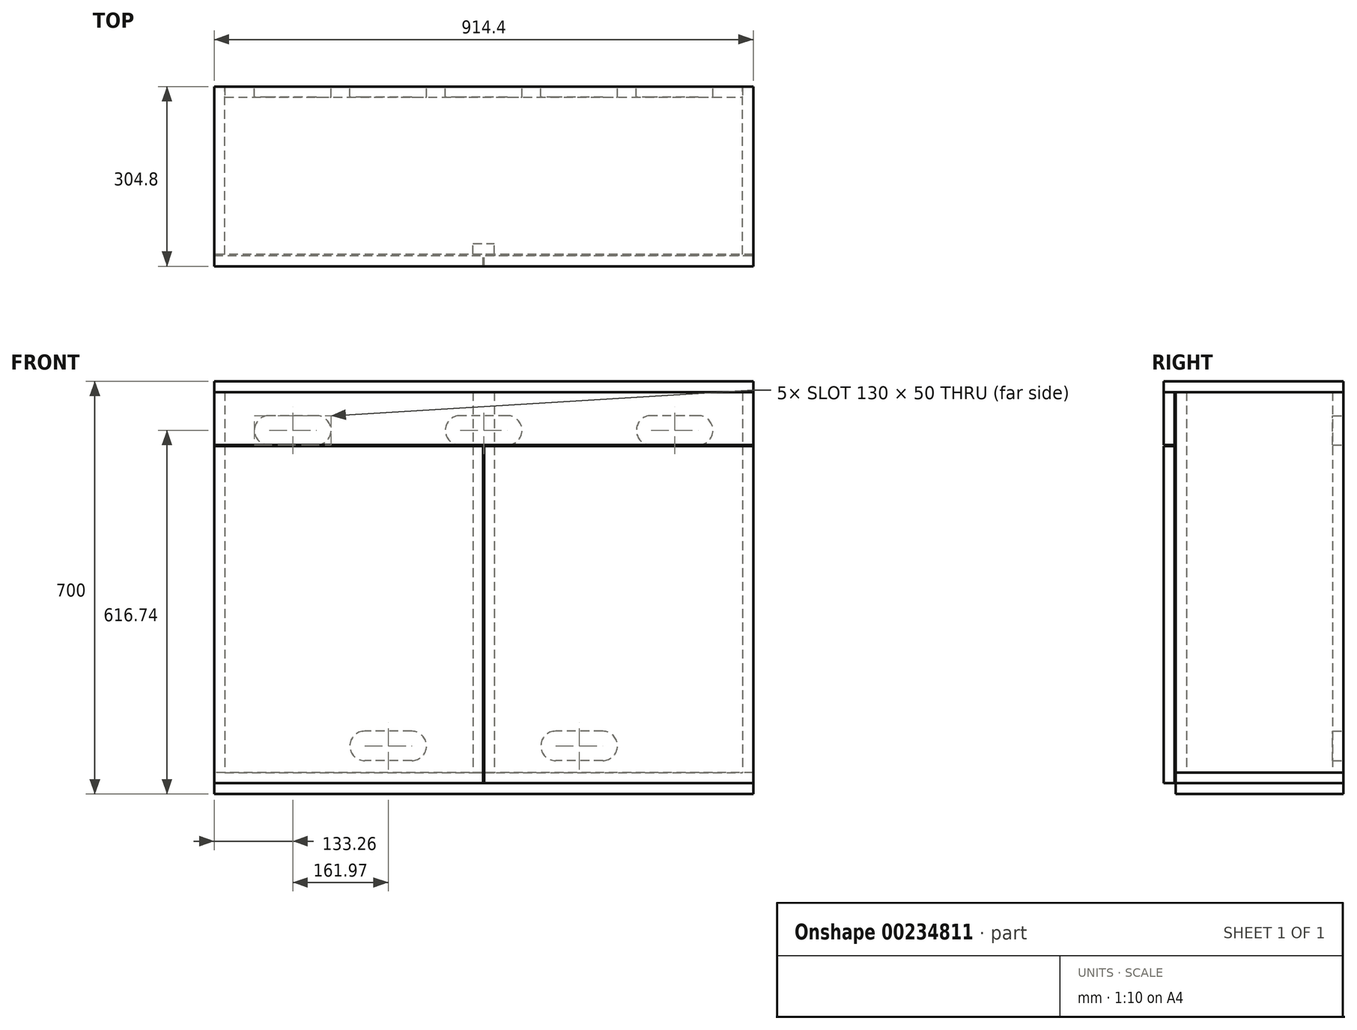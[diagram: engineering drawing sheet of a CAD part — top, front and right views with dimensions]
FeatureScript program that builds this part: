
annotation { "Feature Type Name" : "Feature", "Feature Type Description" : "" }
export const myFeature = defineFeature(function(context is Context, id is Id, definition is map)
    precondition{}
    {
        {
            var Q0;
            Q0=qCreatedBy(makeId("Top.planeOp"),FACE);
            var sketch = newSketch(context, id + "F0", { "sketchPlane" : qUnion([Q0])});
            skLineSegment(sketch, "E0.bottom", {"start": v(457.2, 142.27) * mm, "end": v(-457.2, 142.27) * mm});
            skLineSegment(sketch, "E0.top", {"start": v(457.2, -142.27) * mm, "end": v(-457.2, -142.27) * mm});
            skLineSegment(sketch, "E0.left", {"start": v(457.2, 142.27) * mm, "end": v(457.2, -142.27) * mm});
            skLineSegment(sketch, "E0.right", {"start": v(-457.2, 142.27) * mm, "end": v(-457.2, -142.27) * mm});
            skPoint(sketch, "E0.middle", {"position": v(0, 0) * mm});
            skSolve(sketch);
        }
        {
            var Q0;
            Q0=makeQuery(id+"F0.imprint","IMPRINT",FACE,{"disambiguationData":[TD([[makeQuery(id+"F0.imprint","IMPRINT",EDGE,{"derivedFrom":sQuery(id+"F0.wireOp",EDGE,"E0.bottom")}),1.0]])]});
            extrude(context, id + "F1", {"entities" : qUnion([Q0]), "depth" : 18.26 * mm, "offsetDistance" : 25 * mm});
        }
        {
            var Q0;
            Q0=makeQuery(id+"F1.opExtrude","CAP_FACE",FACE,{"disambiguationData":[OSD([sQuery(id+"F0.wireOp",EDGE,"E0.bottom"),sQuery(id+"F0.wireOp",EDGE,"E0.top"),sQuery(id+"F0.wireOp",EDGE,"E0.left"),sQuery(id+"F0.wireOp",EDGE,"E0.right")])],"isStart":false});
            var sketch = newSketch(context, id + "F2", { "sketchPlane" : qUnion([Q0])});
            skLineSegment(sketch, "E1.bottom", {"start": v(438.94, -142.27) * mm, "end": v(457.2, -142.27) * mm});
            skLineSegment(sketch, "E1.top", {"start": v(438.94, 142.27) * mm, "end": v(457.2, 142.27) * mm});
            skLineSegment(sketch, "E1.left", {"start": v(438.94, -142.27) * mm, "end": v(438.94, 142.27) * mm});
            skLineSegment(sketch, "E1.right", {"start": v(457.2, -142.27) * mm, "end": v(457.2, 142.27) * mm});
            skLineSegment(sketch, "E2.MirrorCS", {"start": v(-438.94, 142.27) * mm, "end": v(-457.2, 142.27) * mm});
            skLineSegment(sketch, "E3.MirrorCS", {"start": v(-438.94, -142.27) * mm, "end": v(-457.2, -142.27) * mm});
            skLineSegment(sketch, "E4.MirrorCS", {"start": v(-457.2, -142.27) * mm, "end": v(-457.2, 142.27) * mm});
            skLineSegment(sketch, "E5.MirrorCS", {"start": v(-438.94, -142.27) * mm, "end": v(-438.94, 142.27) * mm});
            skSolve(sketch);
        }
        {
            var Q0;
            Q0 = qSketchRegion(id + "F2", true);
            extrude(context, id + "F3", {"entities" : qUnion([Q0]), "depth" : 645.22 * mm, "offsetDistance" : 25 * mm});
        }
        {
            var Q0;
            Q0=makeQuery(id+"F1.opExtrude","CAP_FACE",FACE,{"disambiguationData":[OSD([sQuery(id+"F0.wireOp",EDGE,"E0.bottom"),sQuery(id+"F0.wireOp",EDGE,"E0.top"),sQuery(id+"F0.wireOp",EDGE,"E0.left"),sQuery(id+"F0.wireOp",EDGE,"E0.right")])],"isStart":false});
            var sketch = newSketch(context, id + "F4", { "sketchPlane" : qUnion([Q0])});
            skLineSegment(sketch, "E6.bottom", {"start": v(-438.94, 142.27) * mm, "end": v(438.94, 142.27) * mm});
            skLineSegment(sketch, "E6.top", {"start": v(-438.94, 124.01) * mm, "end": v(438.94, 124.01) * mm});
            skLineSegment(sketch, "E6.left", {"start": v(-438.94, 142.27) * mm, "end": v(-438.94, 124.01) * mm});
            skLineSegment(sketch, "E6.right", {"start": v(438.94, 142.27) * mm, "end": v(438.94, 124.01) * mm});
            skSolve(sketch);
        }
        {
            var Q0;
            Q0 = qSketchRegion(id + "F4", true);
            var Q1;
            Q1=makeQuery(id+"F3.opExtrude","CAP_FACE",FACE,{"disambiguationData":[OSD([sQuery(id+"F2.wireOp",EDGE,"E1.bottom"),sQuery(id+"F2.wireOp",EDGE,"E1.top"),sQuery(id+"F2.wireOp",EDGE,"E1.left"),sQuery(id+"F2.wireOp",EDGE,"E1.right")])],"isStart":false});
            extrude(context, id + "F5", {"entities" : qUnion([Q0]), "endBound" : BoundingType.UP_TO_SURFACE, "depth" : 25 * mm, "endBoundEntityFace" : qUnion([Q1]), "offsetDistance" : 25 * mm});
        }
        {
            var Q0;
            Q0=makeQuery(id+"F1.opExtrude","CAP_FACE",FACE,{"disambiguationData":[OSD([sQuery(id+"F0.wireOp",EDGE,"E0.bottom"),sQuery(id+"F0.wireOp",EDGE,"E0.top"),sQuery(id+"F0.wireOp",EDGE,"E0.left"),sQuery(id+"F0.wireOp",EDGE,"E0.right")])],"isStart":false});
            var sketch = newSketch(context, id + "F6", { "sketchPlane" : qUnion([Q0])});
            skLineSegment(sketch, "E7.bottom", {"start": v(-18.26, -142.27) * mm, "end": v(18.26, -142.27) * mm});
            skLineSegment(sketch, "E7.top", {"start": v(-18.26, -124.01) * mm, "end": v(18.26, -124.01) * mm});
            skLineSegment(sketch, "E7.left", {"start": v(-18.26, -142.27) * mm, "end": v(-18.26, -124.01) * mm});
            skLineSegment(sketch, "E7.right", {"start": v(18.26, -142.27) * mm, "end": v(18.26, -124.01) * mm});
            skLineSegment(sketch, "E8", {"start": v(0, 0) * mm, "end": v(0, -142.27) * mm, "construction": true});
            skSolve(sketch);
        }
        {
            var Q0;
            Q0 = qSketchRegion(id + "F6", true);
            var Q1;
            Q1=makeQuery(id+"F5.opExtrude","CAP_FACE",FACE,{"disambiguationData":[OSD([sQuery(id+"F4.wireOp",EDGE,"E6.bottom"),sQuery(id+"F4.wireOp",EDGE,"E6.top"),sQuery(id+"F4.wireOp",EDGE,"E6.left"),sQuery(id+"F4.wireOp",EDGE,"E6.right")])],"isStart":false});
            extrude(context, id + "F7", {"entities" : qUnion([Q0]), "endBound" : BoundingType.UP_TO_SURFACE, "depth" : 25 * mm, "endBoundEntityFace" : qUnion([Q1]), "offsetDistance" : 25 * mm});
        }
        {
            var Q0;
            Q0=makeQuery(id+"F1.opExtrude","CAP_FACE",FACE,{"disambiguationData":[OSD([sQuery(id+"F0.wireOp",EDGE,"E0.bottom"),sQuery(id+"F0.wireOp",EDGE,"E0.top"),sQuery(id+"F0.wireOp",EDGE,"E0.left"),sQuery(id+"F0.wireOp",EDGE,"E0.right")])],"isStart":true});
            extrude(context, id + "F8", {"entities" : qUnion([Q0]), "depth" : 18.26 * mm, "offsetDistance" : 25 * mm});
        }
        {
            var Q0;
            Q0=makeQuery(id+"F3.opExtrude","SWEPT_FACE",FACE,{"disambiguationData":[OSD([sQuery(id+"F2.wireOp",EDGE,"E3.MirrorCS")])]});
            cPlane(context, id + "F9", {"entities" : qUnion([Q0]), "cplaneType" : CPlaneType.OFFSET, "offset" : 2 * mm, "width" : 150 * mm, "height" : 150 * mm});
        }
        {
            var Q0;
            Q0=qCreatedBy(id+"F9.planeOp",FACE);
            var sketch = newSketch(context, id + "F10", { "sketchPlane" : qUnion([Q0])});
            skLineSegment(sketch, "E9.bottom", {"start": v(-457.2, 663.48) * mm, "end": v(457.2, 663.48) * mm});
            skLineSegment(sketch, "E9.top", {"start": v(-457.2, 573.48) * mm, "end": v(457.2, 573.48) * mm});
            skLineSegment(sketch, "E9.left", {"start": v(-457.2, 663.48) * mm, "end": v(-457.2, 573.48) * mm});
            skLineSegment(sketch, "E9.right", {"start": v(457.2, 663.48) * mm, "end": v(457.2, 573.48) * mm});
            skSolve(sketch);
        }
        {
            var Q0;
            Q0 = qSketchRegion(id + "F10", true);
            extrude(context, id + "F11", {"entities" : qUnion([Q0]), "depth" : 18.26 * mm, "offsetDistance" : 25 * mm});
        }
        {
            var Q0;
            Q0=makeQuery(id+"F3.opExtrude","CAP_FACE",FACE,{"disambiguationData":[OSD([sQuery(id+"F2.wireOp",EDGE,"E2.MirrorCS"),sQuery(id+"F2.wireOp",EDGE,"E3.MirrorCS"),sQuery(id+"F2.wireOp",EDGE,"E4.MirrorCS"),sQuery(id+"F2.wireOp",EDGE,"E5.MirrorCS")])],"isStart":false});
            var sketch = newSketch(context, id + "F12", { "sketchPlane" : qUnion([Q0])});
            skLineSegment(sketch, "E10.bottom", {"start": v(-457.2, 142.27) * mm, "end": v(457.2, 142.27) * mm});
            skLineSegment(sketch, "E10.top", {"start": v(-457.2, -162.53) * mm, "end": v(457.2, -162.53) * mm});
            skLineSegment(sketch, "E10.left", {"start": v(-457.2, 142.27) * mm, "end": v(-457.2, -162.53) * mm});
            skLineSegment(sketch, "E10.right", {"start": v(457.2, 142.27) * mm, "end": v(457.2, -162.53) * mm});
            skSolve(sketch);
        }
        {
            var Q0;
            Q0 = qSketchRegion(id + "F12", true);
            extrude(context, id + "F13", {"entities" : qUnion([Q0]), "depth" : 18.26 * mm, "offsetDistance" : 25 * mm});
        }
        {
            var Q0;
            Q0=qCreatedBy(id+"F9.planeOp",FACE);
            var sketch = newSketch(context, id + "F14", { "sketchPlane" : qUnion([Q0])});
            skLineSegment(sketch, "E11.bottom", {"start": v(-457.2, 0) * mm, "end": v(-1, 0) * mm});
            skLineSegment(sketch, "E11.top", {"start": v(-457.2, 571.48) * mm, "end": v(-1, 571.48) * mm});
            skLineSegment(sketch, "E11.left", {"start": v(-457.2, 0) * mm, "end": v(-457.2, 571.48) * mm});
            skLineSegment(sketch, "E11.right", {"start": v(-1, 0) * mm, "end": v(-1, 571.48) * mm});
            skLineSegment(sketch, "E12.MirrorCS", {"start": v(457.2, 0) * mm, "end": v(1, 0) * mm});
            skLineSegment(sketch, "E13.MirrorCS", {"start": v(457.2, 571.48) * mm, "end": v(1, 571.48) * mm});
            skLineSegment(sketch, "E14.MirrorCS", {"start": v(457.2, 0) * mm, "end": v(457.2, 571.48) * mm});
            skLineSegment(sketch, "E15.MirrorCS", {"start": v(1, 0) * mm, "end": v(1, 571.48) * mm});
            skSolve(sketch);
        }
        {
            var Q0;
            Q0 = qSketchRegion(id + "F14", true);
            extrude(context, id + "F15", {"entities" : qUnion([Q0]), "depth" : 18.26 * mm, "offsetDistance" : 25 * mm});
        }
        {
            var Q0;
            Q0=makeQuery(id+"F5.opExtrude","SWEPT_FACE",FACE,{"disambiguationData":[OSD([sQuery(id+"F4.wireOp",EDGE,"E6.bottom")])]});
            var sketch = newSketch(context, id + "F16", { "sketchPlane" : qUnion([Q0])});
            skCircle(sketch, "E16", {"center": v(-363.94, 598.48) * mm, "radius": 25 * mm});
            skCircle(sketch, "E17", {"center": v(-283.94, 598.48) * mm, "radius": 25 * mm});
            skLineSegment(sketch, "E18", {"start": v(-363.94, 623.48) * mm, "end": v(-283.94, 623.48) * mm});
            skLineSegment(sketch, "E19", {"start": v(-363.94, 573.48) * mm, "end": v(-283.94, 573.48) * mm});
            skCircle(sketch, "E20.1.0.0", {"center": v(40, 598.48) * mm, "radius": 25 * mm});
            skLineSegment(sketch, "E20.1.0.1", {"start": v(-40, 573.48) * mm, "end": v(40, 573.48) * mm});
            skLineSegment(sketch, "E20.1.0.2", {"start": v(-40, 623.48) * mm, "end": v(40, 623.48) * mm});
            skCircle(sketch, "E20.1.0.3", {"center": v(-40, 598.48) * mm, "radius": 25 * mm});
            skCircle(sketch, "E20.2.0.0", {"center": v(363.94, 598.48) * mm, "radius": 25 * mm});
            skLineSegment(sketch, "E20.2.0.1", {"start": v(283.94, 573.48) * mm, "end": v(363.94, 573.48) * mm});
            skLineSegment(sketch, "E20.2.0.2", {"start": v(283.94, 623.48) * mm, "end": v(363.94, 623.48) * mm});
            skCircle(sketch, "E20.2.0.3", {"center": v(283.94, 598.48) * mm, "radius": 25 * mm});
            skLineSegment(sketch, "E20.direction1", {"start": v(-363.94, 573.48) * mm, "end": v(-40, 573.48) * mm, "construction": true});
            skCircle(sketch, "E21", {"center": v(121.97, 63.26) * mm, "radius": 25 * mm});
            skCircle(sketch, "E22", {"center": v(201.97, 63.26) * mm, "radius": 25 * mm});
            skLineSegment(sketch, "E23", {"start": v(121.97, 88.26) * mm, "end": v(201.97, 88.26) * mm});
            skLineSegment(sketch, "E24", {"start": v(121.97, 38.26) * mm, "end": v(201.97, 38.26) * mm});
            skLineSegment(sketch, "E25", {"start": v(40, 598.48) * mm, "end": v(283.94, 598.48) * mm, "construction": true});
            skLineSegment(sketch, "E26", {"start": v(161.97, 598.48) * mm, "end": v(161.97, 18.26) * mm, "construction": true});
            skLineSegment(sketch, "E27.1.0.0", {"start": v(-201.97, 38.26) * mm, "end": v(-121.97, 38.26) * mm});
            skLineSegment(sketch, "E27.1.0.1", {"start": v(-201.97, 88.26) * mm, "end": v(-121.97, 88.26) * mm});
            skCircle(sketch, "E27.1.0.2", {"center": v(-121.97, 63.26) * mm, "radius": 25 * mm});
            skCircle(sketch, "E27.1.0.3", {"center": v(-201.97, 63.26) * mm, "radius": 25 * mm});
            skLineSegment(sketch, "E27.direction1", {"start": v(121.97, 38.26) * mm, "end": v(-201.97, 38.26) * mm, "construction": true});
            skSolve(sketch);
        }
        {
            var Q0;
            Q0 = qSketchRegion(id + "F16", true);
            extrude(context, id + "F17", {"entities" : qUnion([Q0]), "operationType" : NewBodyOperationType.REMOVE, "oppositeDirection" : true, "depth" : 25 * mm, "offsetDistance" : 25 * mm});
        }
    });
